# Revit family: DW-2G
name_source: partatom
category: Lighting Fixtures
revit_build: Autodesk Revit 2018 (Build: 20181015_0930(x64)
units: mm (PartAtom-declared; Revit-internal decimal feet)

## family parameters
Always vertical = Yes
Cut with Voids When Loaded = No
Light Source = Yes
OmniClass Number = 23.80.70.00
OmniClass Title = Lighting
Part Type = Normal
Room Calculation Point = No
Round Connector Dimension = Use Diameter
Shared = No
Work Plane-Based = No

## types (8) — shared parameters
Color Filter = 16777215
DW fibreglass = DW fibreglass
DW housing = DW housing
Dimming Lamp Color Temperature Shift = <None>
Emit Shape Visible in Rendering = No
Emit from Rectangle Width = 20 mm  [stored 0.0656168 ft]
Light Source Symbol Size = 100 mm  [stored 0.328084 ft]
die cast alum = die cast alum
die cast aluminium = die cast aluminium
mould latch = mould latch
mount color = mount
mount height = 2700 mm  [stored 8.85827 ft]
voltage = 277 V

## per-type parameters (varying)
| type | Apparent Load | Emit from Rectangle Length | lenght |
| DW -2G 2FT 18 LED | 18 VA | 559 mm | 610 mm |
| DW -2G 2FT 20 LED | 20 VA | 559 mm | 610 mm |
| DW -2G 2FT 27 LED | 27 VA | 559 mm | 610 mm |
| DW -2G 2FT 36 LED | 27 VA | 559 mm | 610 mm |
| DW -2G 4FT 36 LED | 36 VA | 1168 mm | 1219 mm |
| DW -2G 4FT 45 LED | 45 VA | 1168 mm | 1219 mm |
| DW -2G 4FT 56 LED | 56 VA | 1168 mm | 1219 mm |
| DW -2G 4FT 72 LED | 72 VA | 1168 mm | 1219 mm |

note: [stored X ft] marks values corroborated as IEEE doubles in the binary element streams (Revit-internal decimal feet)

## geometry (parser evidence)
native form markers: Sweep x15
no freeform markers — native parametric forms only
